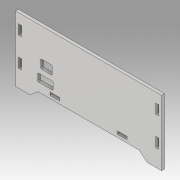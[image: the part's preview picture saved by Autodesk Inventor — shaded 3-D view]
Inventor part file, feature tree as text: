
AUTODESK INVENTOR PART (.ipt)
format: ipt  version: 2019.3 (Build 233278000, 278)  size: 172,032 bytes
history: native  units: mm
features: extrude x2, sketch x2
ambient origin geometry x8: Origin, YZ Plane, XZ Plane, XY Plane, X Axis, Y Axis, Z Axis, Center Point
bodies: Solid1 (feature_tree)
feature tree (4):
  extrude  "Extrusion1"  Depth=10.0mm
  extrude  "Extrusion2"  Depth=10.0mm
  sketch  "Sketch1"  dims[d0=3.0mm d1=10.0mm]
  sketch  "Sketch2"  dims[d2=60.0mm d3=10.0mm d4=152.0mm d5=36.0mm d6=36.0mm d7=3.1mm d8=10.0mm d9=20.0mm d10=5.0mm d11=10.0mm d12=3.0mm d13=3.0mm d14=3.0mm d15=15.0mm d16=15.0mm d17=105.0mm d18=3.0mm d19=0.0mm d20=26.09mm d21=10.0mm d22=0.0mm d23=12.0mm d24=9.0mm d28=20.6mm d29=1.0mm d30=12.75mm d31=37.25mm d32=5.0mm d33=5.0mm d34=16.0mm d35=3.0mm d36=8.0mm d37=1.0mm]
